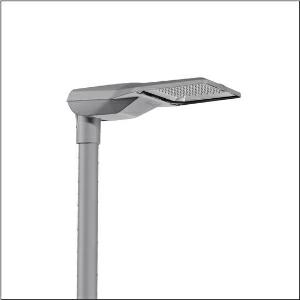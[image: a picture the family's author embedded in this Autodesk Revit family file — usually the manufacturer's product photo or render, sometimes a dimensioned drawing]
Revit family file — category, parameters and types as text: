
# Revit family: streetlight_sl_21_iq_midi___st0_5a_5xe3b41d08nb_db24
name_source: partatom
category: Lighting Fixtures
units: mm (PartAtom-declared; Revit-internal decimal feet)

## family parameters
Cut with Voids When Loaded = No
Host = Face
Light Source = No
Part Type = Normal
Room Calculation Point = No
Round Connector Dimension = Use Diameter
Shared = No

## types (1)
- --- (1 x LED, 24250 lm, 155.5 W, 4000K)
    Apparent Load = 155 VA
    CIE Flux Codes = 43 76 97 100 100
    Color Rendering = 70
    Color Temperature = 4000K
    Default Elevation = 1800 mm
    Description = Streetlight SL 21 iQ midi, mast luminaire, primary light control with lens, of PMMA, primary optical cover: cover, of toughened safety glass, transparent, light distribution: ST0.5a, light emission: direct distribution, primary light characteristic: asymmetric, installation type: post-top, side-entry, LED, High Power LED, rated luminous flux: 24.250lm, luminous efficacy: 156lm/W, light colour: 740, colour temperature: 4000K, control: Auto-Match, Temp-Guard, Lumen-Switch, Night-Set, Smart-Wire, Light-Fading, Desk-Remote (wireless, voltage-free reading and setting of iQ features in the workshop via application-optimized NFC function/RFID function), optimised constant luminous flux control (CLO 2.0), presetting dimming linear, mains connection: 230..240V, AC, 50/60Hz, start of lifetime: 156W, end of service life: 162W, reduction: 69W, luminaire housing, of diecast aluminium, powder-coated, Siteco® metallic grey (DB 702S), corrosivity category C5 mid according to DIN EN ISO 12944, please order mast flange separately, inclination adjustable: 0°, 5°, 10°, 15°, sealing non-destructively replaceable, multi-level sealing system, length: 644mm, width: 335mm, height: 110mm, mast flange for spigot size: 42mm (side-entry): 5XC10008XM4, 60/48mm (side-entry/post-top): 5XC10108XM2, 76/60mm (side-entry/post-top): 5XC10108XM1, protection rating (complete): IP66, insulation class (complete): insulation class II (safety insulation), certification: CE, ENEC, ENEC+, VDE, impact resistance: IK09, permissible operating ambient temperature for outdoor applications: -40..+50°C, standard-compliant lighting for roads and squares, packaging unit: 1 piece

Light Distribution: ST0.5a
    Height = 111 mm
    Lamp = 1 x LED
    Lamp Light Flux = 24250 lm
    Lamp Power = 155.5 W
    Lamp count = 1
    Length = 644 mm
    Luminous efficacy = 156 lm/W
    Manufacturer = Siteco
    ModVariant = No
    Model = 5XE3B41D08NB
    Number of Poles = 1
    OnlyDefault = Yes
    Power Factor = 1
    Product Name = Streetlight SL 21 iQ midi | ST0.5a
    Product group = mast luminaire | pylon top
    ProductGroupID = 6100
    Protection Class = Protection class II
    Protection Degree = IP 66
    RLX_Detail_Level = 1
    RLX_Emergency_Light_Flux = 0 lm
    RLX_Emergency_Type = 0
    RLX_Emergency_Type_DB = No
    RlxData = <blob elided: 102145 chars, md5=fb3d8b8b>
    Socket = socket
    Standby Power = 0 W
    System Light Flux = 24250 lm
    System Power = 155 W
    Type Comments = factory setting: luminous flux: 100 % | dim-lin: 254 | 823 mA
    Type Image = l_1004298.jpg
    URL = http://relux.com
    VarID = @adj_122281
    Voltage = 0 V
    Weight = 0.00 kg
    Width = 336 mm

## geometry (parser evidence)
native form markers: Blend x4, Sweep x11
no freeform markers — native parametric forms only
